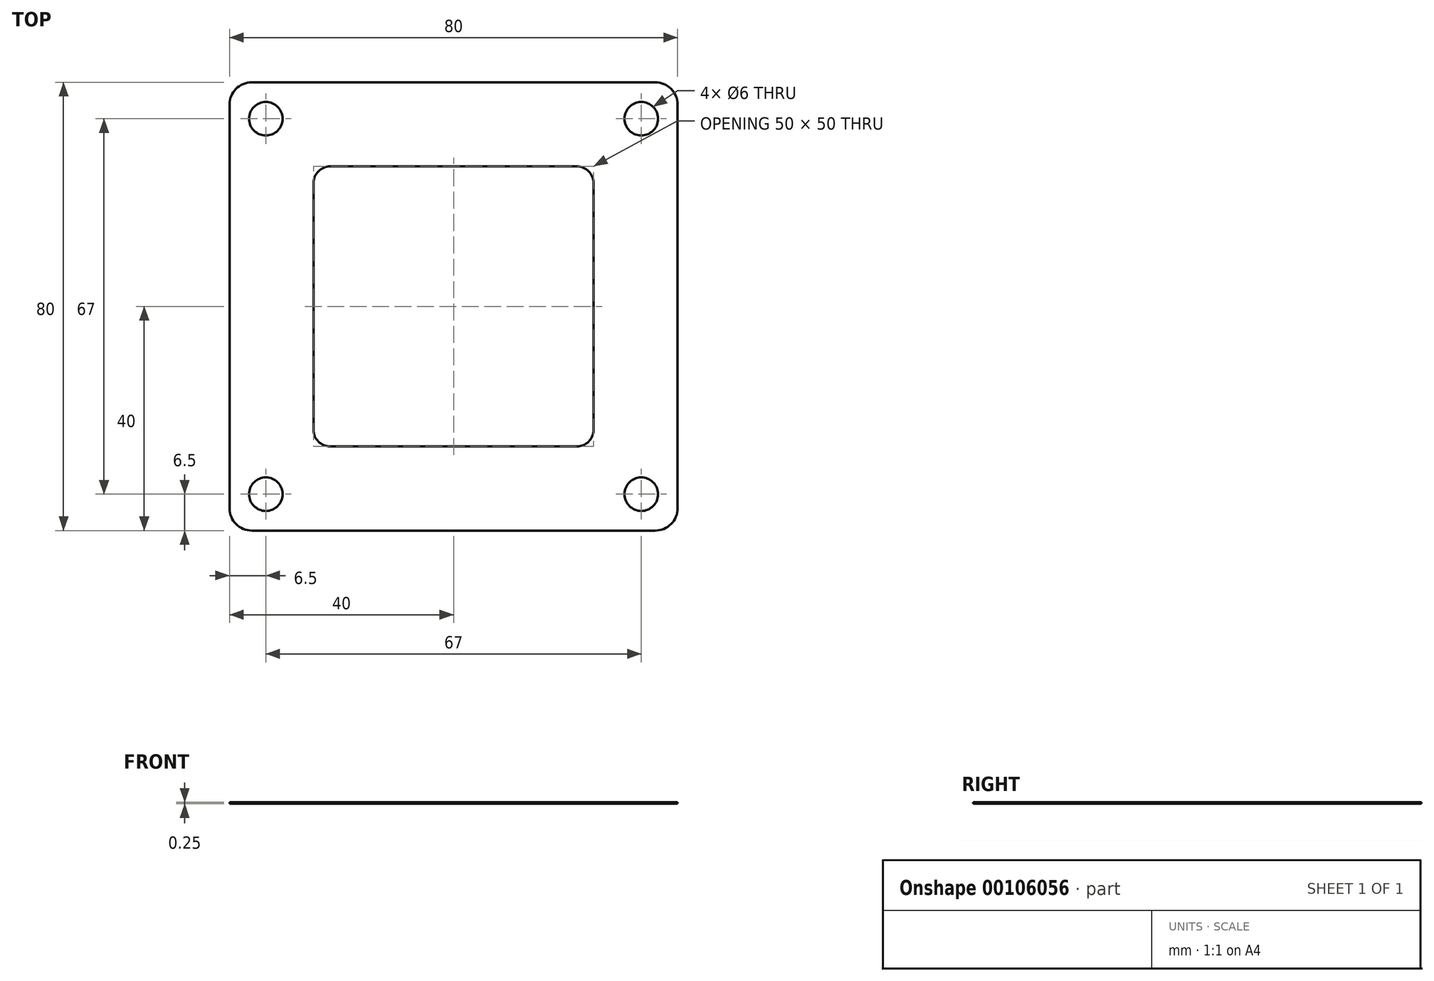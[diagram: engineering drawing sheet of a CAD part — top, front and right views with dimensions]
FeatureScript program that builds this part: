
annotation { "Feature Type Name" : "Feature", "Feature Type Description" : "" }
export const myFeature = defineFeature(function(context is Context, id is Id, definition is map)
    precondition{}
    {
        {
            var Q0;
            Q0=qCreatedBy(makeId("Top.planeOp"),FACE);
            var sketch = newSketch(context, id + "F0", { "sketchPlane" : qUnion([Q0])});
            skLineSegment(sketch, "E0.bottom", {"start": v(4, 0) * mm, "end": v(76, 0) * mm});
            skLineSegment(sketch, "E0.top", {"start": v(4, 80) * mm, "end": v(76, 80) * mm});
            skLineSegment(sketch, "E0.left", {"start": v(0, 4) * mm, "end": v(0, 76) * mm});
            skLineSegment(sketch, "E0.right", {"start": v(80, 4) * mm, "end": v(80, 76) * mm});
            skPoint(sketch, "E1.visualSharp", {"position": v(0, 80) * mm});
            skArc(sketch, "E1.filletArc", {"start": v(4, 80) * mm, "mid": v(1.17, 78.83) * mm, "end": v(0, 76) * mm});
            skPoint(sketch, "E2.visualSharp", {"position": v(80, 80) * mm});
            skArc(sketch, "E2.filletArc", {"start": v(80, 76) * mm, "mid": v(78.83, 78.83) * mm, "end": v(76, 80) * mm});
            skPoint(sketch, "E3.visualSharp", {"position": v(80, 0) * mm});
            skArc(sketch, "E3.filletArc", {"start": v(76, 0) * mm, "mid": v(78.83, 1.17) * mm, "end": v(80, 4) * mm});
            skPoint(sketch, "E4.visualSharp", {"position": v(0, 0) * mm});
            skArc(sketch, "E4.filletArc", {"start": v(0, 4) * mm, "mid": v(1.17, 1.17) * mm, "end": v(4, 0) * mm});
            skLineSegment(sketch, "E5.bottom", {"start": v(18, 65) * mm, "end": v(62, 65) * mm});
            skLineSegment(sketch, "E5.top", {"start": v(18, 15) * mm, "end": v(62, 15) * mm});
            skLineSegment(sketch, "E5.left", {"start": v(15, 62) * mm, "end": v(15, 18) * mm});
            skLineSegment(sketch, "E5.right", {"start": v(65, 62) * mm, "end": v(65, 18) * mm});
            skPoint(sketch, "E6.visualSharp", {"position": v(15, 65) * mm});
            skArc(sketch, "E6.filletArc", {"start": v(18, 65) * mm, "mid": v(15.88, 64.12) * mm, "end": v(15, 62) * mm});
            skPoint(sketch, "E7.visualSharp", {"position": v(65, 65) * mm});
            skArc(sketch, "E7.filletArc", {"start": v(65, 62) * mm, "mid": v(64.12, 64.12) * mm, "end": v(62, 65) * mm});
            skPoint(sketch, "E8.visualSharp", {"position": v(65, 15) * mm});
            skArc(sketch, "E8.filletArc", {"start": v(62, 15) * mm, "mid": v(64.12, 15.88) * mm, "end": v(65, 18) * mm});
            skPoint(sketch, "E9.visualSharp", {"position": v(15, 15) * mm});
            skArc(sketch, "E9.filletArc", {"start": v(15, 18) * mm, "mid": v(15.88, 15.88) * mm, "end": v(18, 15) * mm});
            skCircle(sketch, "E10", {"center": v(6.5, 73.5) * mm, "radius": 3 * mm});
            skCircle(sketch, "E11.0.1.0", {"center": v(6.5, 6.5) * mm, "radius": 3 * mm});
            skCircle(sketch, "E11.1.0.0", {"center": v(73.5, 73.5) * mm, "radius": 3 * mm});
            skCircle(sketch, "E11.1.1.0", {"center": v(73.5, 6.5) * mm, "radius": 3 * mm});
            skLineSegment(sketch, "E11.direction1", {"start": v(6.5, 73.5) * mm, "end": v(73.5, 73.5) * mm, "construction": true});
            skLineSegment(sketch, "E11.direction2", {"start": v(6.5, 73.5) * mm, "end": v(6.5, 6.5) * mm, "construction": true});
            skSolve(sketch);
        }
        {
            var Q0;
            Q0=makeQuery(id+"F0.imprint","IMPRINT",FACE,{"disambiguationData":[TD([[makeQuery(id+"F0.imprint","IMPRINT",EDGE,{"derivedFrom":sQuery(id+"F0.wireOp",EDGE,"E0.bottom")}),1.0]])]});
            extrude(context, id + "F1", {"entities" : qUnion([Q0]), "depth" : 0.25 * mm});
        }
    });
